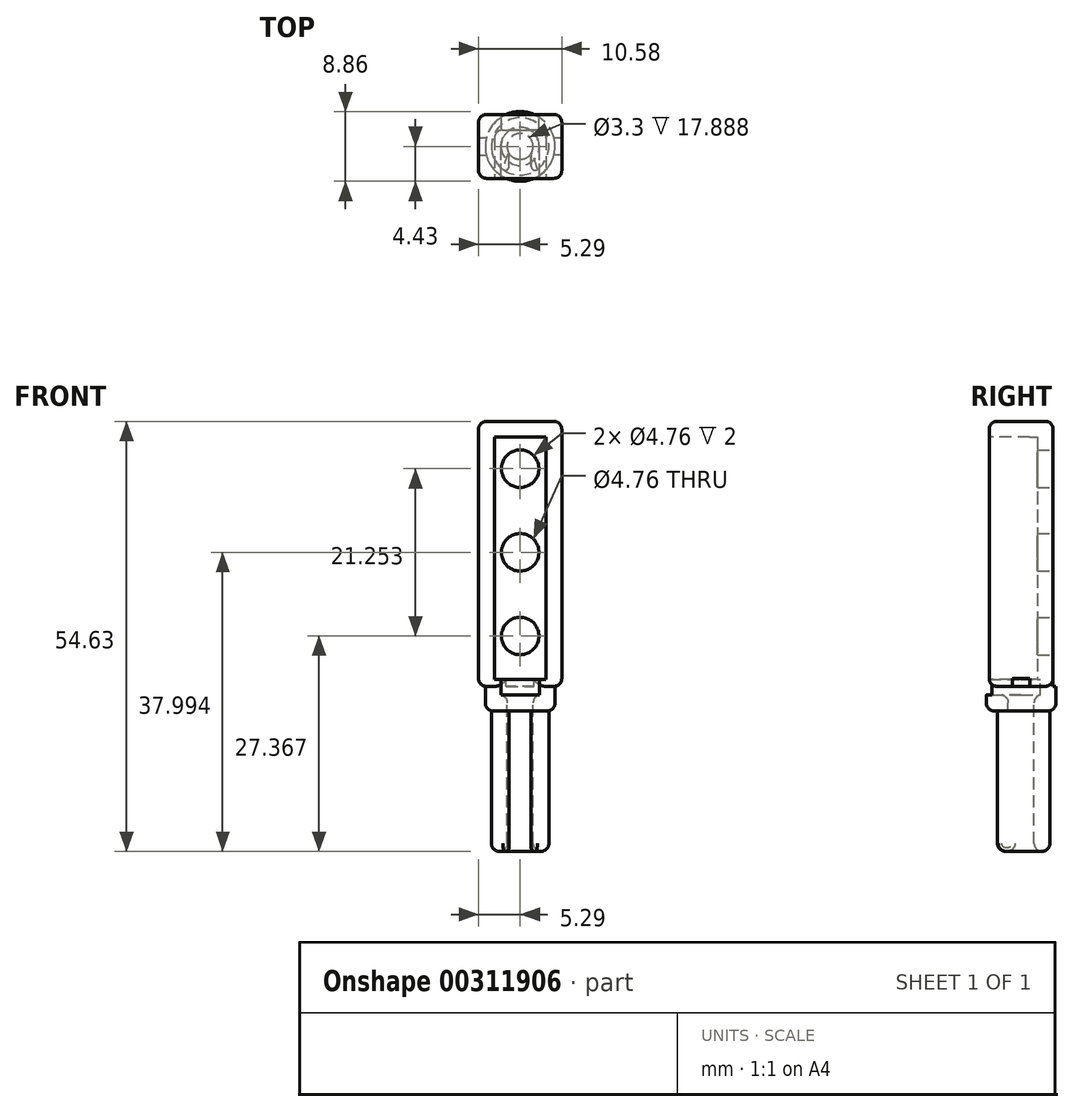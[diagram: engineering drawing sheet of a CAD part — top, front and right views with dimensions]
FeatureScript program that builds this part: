
annotation { "Feature Type Name" : "Feature", "Feature Type Description" : "" }
export const myFeature = defineFeature(function(context is Context, id is Id, definition is map)
    precondition{}
    {
        {
            var Q0;
            Q0=qCreatedBy(makeId("Front.planeOp"),FACE);
            var sketch = newSketch(context, id + "F0", { "sketchPlane" : qUnion([Q0])});
            skLineSegment(sketch, "E0.bottom", {"start": v(-3.3, 14.53) * mm, "end": v(3.3, 14.53) * mm});
            skLineSegment(sketch, "E0.top", {"start": v(-3.29, -16.27) * mm, "end": v(3.29, -16.27) * mm});
            skLineSegment(sketch, "E0.left", {"start": v(-3.3, 14.53) * mm, "end": v(-3.29, -16.27) * mm});
            skLineSegment(sketch, "E0.right", {"start": v(3.3, 14.53) * mm, "end": v(3.29, -16.27) * mm});
            skLineSegment(sketch, "E1.bottom", {"start": v(-2.43, -16.27) * mm, "end": v(2.43, -16.27) * mm});
            skLineSegment(sketch, "E1.top", {"start": v(-2.43, -18.23) * mm, "end": v(2.43, -18.23) * mm});
            skLineSegment(sketch, "E1.left", {"start": v(-2.43, -16.27) * mm, "end": v(-2.43, -18.23) * mm});
            skLineSegment(sketch, "E1.right", {"start": v(2.43, -16.27) * mm, "end": v(2.43, -18.23) * mm});
            skLineSegment(sketch, "E2.bottom", {"start": v(-1.65, -18.23) * mm, "end": v(1.65, -18.23) * mm});
            skLineSegment(sketch, "E2.top", {"start": v(-1.65, -38.23) * mm, "end": v(1.65, -38.23) * mm});
            skLineSegment(sketch, "E2.left", {"start": v(-1.65, -18.23) * mm, "end": v(-1.65, -38.23) * mm});
            skLineSegment(sketch, "E2.right", {"start": v(1.65, -18.23) * mm, "end": v(1.65, -38.23) * mm});
            skLineSegment(sketch, "E3.bottom", {"start": v(-5.29, 16.53) * mm, "end": v(5.3, 16.53) * mm});
            skLineSegment(sketch, "E3.top", {"start": v(-5.29, -17.13) * mm, "end": v(5.3, -17.13) * mm});
            skLineSegment(sketch, "E3.left", {"start": v(-5.3, 16.53) * mm, "end": v(-5.29, -17.13) * mm});
            skLineSegment(sketch, "E3.right", {"start": v(5.29, 16.53) * mm, "end": v(5.3, -17.13) * mm});
            skLineSegment(sketch, "E4.bottom", {"start": v(-4.43, -16.27) * mm, "end": v(4.43, -16.27) * mm});
            skLineSegment(sketch, "E4.top", {"start": v(-4.43, -20.23) * mm, "end": v(4.43, -20.23) * mm});
            skLineSegment(sketch, "E4.left", {"start": v(-4.43, -16.27) * mm, "end": v(-4.43, -20.23) * mm});
            skLineSegment(sketch, "E4.right", {"start": v(4.43, -16.27) * mm, "end": v(4.43, -20.23) * mm});
            skLineSegment(sketch, "E5.bottom", {"start": v(-3.65, -20.23) * mm, "end": v(3.65, -20.23) * mm});
            skLineSegment(sketch, "E5.top", {"start": v(-3.65, -38.1) * mm, "end": v(3.65, -38.1) * mm});
            skLineSegment(sketch, "E5.left", {"start": v(-3.65, -20.23) * mm, "end": v(-3.65, -38.1) * mm});
            skLineSegment(sketch, "E5.right", {"start": v(3.65, -20.23) * mm, "end": v(3.65, -38.1) * mm});
            skLineSegment(sketch, "E6", {"start": v(0, -14.74) * mm, "end": v(0, -39.5) * mm});
            skPoint(sketch, "E6.endSnap0", {"position": v(0, -38.23) * mm});
            skLineSegment(sketch, "E7.bottom", {"start": v(-1.4, -20.23) * mm, "end": v(1.4, -20.23) * mm});
            skLineSegment(sketch, "E7.top", {"start": v(-1.4, -38.1) * mm, "end": v(1.4, -38.1) * mm});
            skLineSegment(sketch, "E7.left", {"start": v(-1.4, -20.23) * mm, "end": v(-1.4, -38.1) * mm});
            skLineSegment(sketch, "E7.right", {"start": v(1.4, -20.23) * mm, "end": v(1.4, -38.1) * mm});
            skSolve(sketch);
        }
        {
            var Q0;
            Q0=makeQuery(id+"F0.imprint","IMPRINT",FACE,{"disambiguationData":[TD([[makeQuery(id+"F0.imprint","IMPRINT",EDGE,{"derivedFrom":sQuery(id+"F0.wireOp",EDGE,"E0.bottom")}),-1.0]])]});
            var Q1;
            Q1=makeQuery(id+"F0.imprint","IMPRINT",FACE,{"disambiguationData":[TD([[makeQuery(id+"F0.imprint","IMPRINT",EDGE,{"derivedFrom":sQuery(id+"F0.wireOp",EDGE,"E0.bottom")}),1.0]])]});
            var Q2;
            {var subQ0=sQuery(id+"F0.wireOp",EDGE,"E4.bottom");var subQ2=sQuery(id+"F0.wireOp",EDGE,"E1.left");var subQ3=makeQuery(id+"F0.imprint","INTERSECT",VERTEX,{"derivedFrom":[subQ2,subQ0]});Q2=makeQuery(id+"F0.imprint","IMPRINT",FACE,{"disambiguationData":[TD([[makeQuery(id+"F0.imprint","IMPRINT",EDGE,{"disambiguationData":[TD([[subQ3,-1.0]])],"derivedFrom":subQ2}),-1.0]])]});}
            var Q3;
            {var subQ0=sQuery(id+"F0.wireOp",EDGE,"E4.bottom");var subQ1=sQuery(id+"F0.wireOp",EDGE,"E1.left");var subQ2=makeQuery(id+"F0.imprint","INTERSECT",VERTEX,{"derivedFrom":[subQ1,subQ0]});Q3=makeQuery(id+"F0.imprint","IMPRINT",FACE,{"disambiguationData":[TD([[makeQuery(id+"F0.imprint","IMPRINT",EDGE,{"disambiguationData":[TD([[subQ2,-1.0]])],"derivedFrom":subQ1}),1.0]])]});}
            var Q4;
            {var subQ0=sQuery(id+"F0.wireOp",EDGE,"E4.bottom");var subQ1=sQuery(id+"F0.wireOp",EDGE,"E1.right");var subQ2=makeQuery(id+"F0.imprint","INTERSECT",VERTEX,{"derivedFrom":[subQ1,subQ0]});Q4=makeQuery(id+"F0.imprint","IMPRINT",FACE,{"disambiguationData":[TD([[makeQuery(id+"F0.imprint","IMPRINT",EDGE,{"disambiguationData":[TD([[subQ2,-1.0]])],"derivedFrom":subQ1}),-1.0]])]});}
            var Q5;
            {var subQ0=sQuery(id+"F0.wireOp",EDGE,"E4.bottom");var subQ6=sQuery(id+"F0.wireOp",EDGE,"E1.right");var subQ8=makeQuery(id+"F0.imprint","INTERSECT",VERTEX,{"derivedFrom":[subQ6,subQ0]});Q5=makeQuery(id+"F0.imprint","IMPRINT",FACE,{"disambiguationData":[TD([[makeQuery(id+"F0.imprint","IMPRINT",EDGE,{"disambiguationData":[TD([[subQ8,-1.0]])],"derivedFrom":subQ6}),1.0]])]});}
            extrude(context, id + "F1", {"entities" : qUnion([Q0, Q1, Q2, Q3, Q4, Q5]), "endBound" : BoundingType.SYMMETRIC, "depth" : 8.12 * mm});
        }
        {
            var Q0;
            Q0=makeQuery(id+"F1.opExtrude","CAP_FACE",FACE,{"disambiguationData":[OSD([sQuery(id+"F0.wireOp",EDGE,"E1.bottom"),sQuery(id+"F0.wireOp",EDGE,"E1.left"),sQuery(id+"F0.wireOp",EDGE,"E1.right"),sQuery(id+"F0.wireOp",EDGE,"E3.bottom"),sQuery(id+"F0.wireOp",EDGE,"E3.top"),sQuery(id+"F0.wireOp",EDGE,"E3.left"),sQuery(id+"F0.wireOp",EDGE,"E3.right")])],"isStart":false});
            var sketch = newSketch(context, id + "F2", { "sketchPlane" : qUnion([Q0])});
            skLineSegment(sketch, "E8.bottom", {"start": v(-3.26, 14.52) * mm, "end": v(3.3, 14.52) * mm});
            skLineSegment(sketch, "E8.top", {"start": v(-3.26, -16.27) * mm, "end": v(3.3, -16.27) * mm});
            skLineSegment(sketch, "E8.left", {"start": v(-3.26, 14.52) * mm, "end": v(-3.26, -16.27) * mm});
            skLineSegment(sketch, "E8.right", {"start": v(3.3, 14.52) * mm, "end": v(3.3, -16.27) * mm});
            skSolve(sketch);
        }
        {
            var Q0;
            Q0=makeQuery(id+"F2.imprint","IMPRINT",FACE,{"disambiguationData":[TD([[makeQuery(id+"F2.imprint","IMPRINT",EDGE,{"derivedFrom":sQuery(id+"F2.wireOp",EDGE,"E8.bottom")}),-1.0]])]});
            extrude(context, id + "F3", {"entities" : qUnion([Q0]), "operationType" : NewBodyOperationType.REMOVE, "oppositeDirection" : true, "depth" : 6.12 * mm});
        }
        {
            var Q0;
            {var subQ3=sQuery(id+"F0.wireOp",EDGE,"E1.left");var subQ5=sQuery(id+"F0.wireOp",EDGE,"E1.top");var subQ6=makeQuery(id+"F0.imprint","INTERSECT",VERTEX,{"derivedFrom":[subQ5,subQ3]});Q0=makeQuery(id+"F0.imprint","IMPRINT",FACE,{"disambiguationData":[TD([[makeQuery(id+"F0.imprint","IMPRINT",EDGE,{"disambiguationData":[TD([[subQ6,1.0]])],"derivedFrom":subQ3}),-1.0]])]});}
            var Q1;
            {var subQ1=sQuery(id+"F0.wireOp",EDGE,"E1.top");var subQ5=sQuery(id+"F0.wireOp",EDGE,"E1.right");var subQ6=makeQuery(id+"F0.imprint","INTERSECT",VERTEX,{"derivedFrom":[subQ1,subQ5]});Q1=makeQuery(id+"F0.imprint","IMPRINT",FACE,{"disambiguationData":[TD([[makeQuery(id+"F0.imprint","IMPRINT",EDGE,{"disambiguationData":[TD([[subQ6,1.0]])],"derivedFrom":subQ5}),1.0]])]});}
            var Q2;
            {var subQ5=sQuery(id+"F0.wireOp",EDGE,"E5.right");Q2=makeQuery(id+"F0.imprint","IMPRINT",FACE,{"disambiguationData":[TD([[makeQuery(id+"F0.imprint","IMPRINT",EDGE,{"derivedFrom":subQ5}),-1.0]])]});}
            var Q3;
            {var subQ5=sQuery(id+"F0.wireOp",EDGE,"E5.left");Q3=makeQuery(id+"F0.imprint","IMPRINT",FACE,{"disambiguationData":[TD([[makeQuery(id+"F0.imprint","IMPRINT",EDGE,{"derivedFrom":subQ5}),1.0]])]});}
            var Q4;
            Q4=sQuery(id+"F0.wireOp",EDGE,"E6");
            revolve(context, id + "F4", {"operationType" : NewBodyOperationType.ADD, "entities" : qUnion([Q0, Q1, Q2, Q3]), "axis" : qUnion([Q4]), "revolveType" : RevolveType.FULL});
        }
        {
            var Q0;
            {var subQ0=sQuery(id+"F0.wireOp",EDGE,"E4.bottom");var subQ1=sQuery(id+"F0.wireOp",EDGE,"E1.left");var subQ2=makeQuery(id+"F0.imprint","INTERSECT",VERTEX,{"derivedFrom":[subQ1,subQ0]});Q0=makeQuery(id+"F0.imprint","IMPRINT",FACE,{"disambiguationData":[TD([[makeQuery(id+"F0.imprint","IMPRINT",EDGE,{"disambiguationData":[TD([[subQ2,-1.0]])],"derivedFrom":subQ1}),1.0]])]});}
            var Q1;
            {var subQ1=sQuery(id+"F0.wireOp",EDGE,"E1.left");var subQ6=sQuery(id+"F0.wireOp",EDGE,"E1.top");var subQ9=makeQuery(id+"F0.imprint","INTERSECT",VERTEX,{"derivedFrom":[subQ6,subQ1]});Q1=makeQuery(id+"F0.imprint","IMPRINT",FACE,{"disambiguationData":[TD([[makeQuery(id+"F0.imprint","IMPRINT",EDGE,{"disambiguationData":[TD([[subQ9,1.0]])],"derivedFrom":subQ1}),1.0]])]});}
            var Q2;
            {var subQ0=sQuery(id+"F0.wireOp",EDGE,"E2.left");var subQ5=sQuery(id+"F0.wireOp",EDGE,"E5.bottom");var subQ6=makeQuery(id+"F0.imprint","INTERSECT",VERTEX,{"derivedFrom":[subQ0,subQ5]});Q2=makeQuery(id+"F0.imprint","IMPRINT",FACE,{"disambiguationData":[TD([[makeQuery(id+"F0.imprint","IMPRINT",EDGE,{"disambiguationData":[TD([[subQ6,-1.0]])],"derivedFrom":subQ5}),1.0]])]});}
            var Q3;
            {var subQ0=sQuery(id+"F0.wireOp",EDGE,"E5.top");var subQ1=sQuery(id+"F0.wireOp",EDGE,"E2.left");var subQ2=makeQuery(id+"F0.imprint","INTERSECT",VERTEX,{"derivedFrom":[subQ1,subQ0]});Q3=makeQuery(id+"F0.imprint","IMPRINT",FACE,{"disambiguationData":[TD([[makeQuery(id+"F0.imprint","IMPRINT",EDGE,{"disambiguationData":[TD([[subQ2,1.0]])],"derivedFrom":subQ1}),1.0]])]});}
            var Q4;
            Q4=sQuery(id+"F0.wireOp",EDGE,"E6");
            revolve(context, id + "F5", {"operationType" : NewBodyOperationType.REMOVE, "entities" : qUnion([Q0, Q1, Q2, Q3]), "axis" : qUnion([Q4]), "revolveType" : RevolveType.FULL, "oppositeDirection" : true});
        }
        {
            var Q0;
            Q0=makeQuery(id+"F3.boolean.opBoolean","COPY",EDGE,{"derivedFrom":makeQuery(id+"F3.opExtrude","CAP_EDGE",EDGE,{"disambiguationData":[OSD([sQuery(id+"F2.wireOp",EDGE,"E8.right")])],"isStart":false})});
            var Q1;
            Q1=makeQuery(id+"F3.boolean.opBoolean","COPY",EDGE,{"derivedFrom":makeQuery(id+"F3.opExtrude","CAP_EDGE",EDGE,{"disambiguationData":[OSD([sQuery(id+"F2.wireOp",EDGE,"E8.left")])],"isStart":false})});
            var Q2;
            Q2=makeQuery(id+"FeuInIf9HhXsNGS_0.boolean.opBoolean","INTERSECT",EDGE,{"derivedFrom":[makeQuery(id+"F4.opRevolve","SWEPT_FACE",FACE,{"disambiguationData":[OSD([sQuery(id+"F0.wireOp",EDGE,"E4.left")])]}),makeQuery(id+"FeuInIf9HhXsNGS_0.opExtrude","SWEPT_FACE",FACE,{"disambiguationData":[OSD([sQuery(id+"F0.wireOp",EDGE,"E2.right")])]})]});
            var Q3;
            Q3=makeQuery(id+"FeuInIf9HhXsNGS_0.boolean.opBoolean","INTERSECT",EDGE,{"derivedFrom":[makeQuery(id+"F4.opRevolve","SWEPT_FACE",FACE,{"disambiguationData":[OSD([sQuery(id+"F0.wireOp",EDGE,"E4.left")])]}),makeQuery(id+"FeuInIf9HhXsNGS_0.opExtrude","SWEPT_FACE",FACE,{"disambiguationData":[OSD([sQuery(id+"F0.wireOp",EDGE,"E2.left")])]})]});
            var Q4;
            Q4=makeQuery(id+"F4.opRevolve","SWEPT_EDGE",EDGE,{"disambiguationData":[OSD([sQuery(id+"F0.wireOp",EDGE,"E5.top"),sQuery(id+"F0.wireOp",EDGE,"E5.left")])]});
            var Q5;
            Q5=makeQuery(id+"F4.opRevolve","SWEPT_EDGE",EDGE,{"disambiguationData":[OSD([sQuery(id+"F0.wireOp",EDGE,"E2.left"),sQuery(id+"F0.wireOp",EDGE,"E5.top")])]});
            var Q6;
            Q6=makeQuery(id+"F4.opRevolve","SWEPT_EDGE",EDGE,{"disambiguationData":[OSD([sQuery(id+"F0.wireOp",EDGE,"E4.top"),sQuery(id+"F0.wireOp",EDGE,"E4.left")])]});
            var Q7;
            Q7=makeQuery(id+"F4.opRevolve","SWEPT_EDGE",EDGE,{"disambiguationData":[OSD([sQuery(id+"F0.wireOp",EDGE,"E1.top"),sQuery(id+"F0.wireOp",EDGE,"E2.bottom"),sQuery(id+"F0.wireOp",EDGE,"E2.left")])]});
            fillet(context, id + "F6", {"entities" : qUnion([Q0, Q1, Q2, Q3, Q4, Q5, Q6, Q7]), "radius" : 1 * mm, "tangentPropagation" : true, "allowEdgeOverflow" : false});
        }
        {
            var Q0;
            {var subQ0=sQuery(id+"F0.wireOp",EDGE,"E4.bottom");var subQ1=sQuery(id+"F0.wireOp",EDGE,"E1.left");var subQ2=makeQuery(id+"F0.imprint","INTERSECT",VERTEX,{"derivedFrom":[subQ1,subQ0]});Q0=makeQuery(id+"F0.imprint","IMPRINT",FACE,{"disambiguationData":[TD([[makeQuery(id+"F0.imprint","IMPRINT",EDGE,{"disambiguationData":[TD([[subQ2,-1.0]])],"derivedFrom":subQ1}),1.0]])]});}
            var Q1;
            {var subQ1=sQuery(id+"F0.wireOp",EDGE,"E1.left");var subQ6=sQuery(id+"F0.wireOp",EDGE,"E1.top");var subQ9=makeQuery(id+"F0.imprint","INTERSECT",VERTEX,{"derivedFrom":[subQ6,subQ1]});Q1=makeQuery(id+"F0.imprint","IMPRINT",FACE,{"disambiguationData":[TD([[makeQuery(id+"F0.imprint","IMPRINT",EDGE,{"disambiguationData":[TD([[subQ9,1.0]])],"derivedFrom":subQ1}),1.0]])]});}
            var Q2;
            {var subQ1=sQuery(id+"F0.wireOp",EDGE,"E1.top");var subQ6=sQuery(id+"F0.wireOp",EDGE,"E1.right");var subQ9=makeQuery(id+"F0.imprint","INTERSECT",VERTEX,{"derivedFrom":[subQ1,subQ6]});Q2=makeQuery(id+"F0.imprint","IMPRINT",FACE,{"disambiguationData":[TD([[makeQuery(id+"F0.imprint","IMPRINT",EDGE,{"disambiguationData":[TD([[subQ9,1.0]])],"derivedFrom":subQ6}),-1.0]])]});}
            var Q3;
            {var subQ0=sQuery(id+"F0.wireOp",EDGE,"E4.bottom");var subQ1=sQuery(id+"F0.wireOp",EDGE,"E1.right");var subQ2=makeQuery(id+"F0.imprint","INTERSECT",VERTEX,{"derivedFrom":[subQ1,subQ0]});Q3=makeQuery(id+"F0.imprint","IMPRINT",FACE,{"disambiguationData":[TD([[makeQuery(id+"F0.imprint","IMPRINT",EDGE,{"disambiguationData":[TD([[subQ2,-1.0]])],"derivedFrom":subQ1}),-1.0]])]});}
            var Q4;
            {var subQ0=sQuery(id+"F0.wireOp",EDGE,"E6");var subQ1=sQuery(id+"F0.wireOp",EDGE,"E2.bottom");var subQ2=makeQuery(id+"F0.imprint","INTERSECT",VERTEX,{"derivedFrom":[subQ1,subQ0]});Q4=makeQuery(id+"F0.imprint","IMPRINT",FACE,{"disambiguationData":[TD([[makeQuery(id+"F0.imprint","IMPRINT",EDGE,{"disambiguationData":[TD([[subQ2,-1.0]])],"derivedFrom":subQ0}),1.0]])]});}
            var Q5;
            {var subQ0=sQuery(id+"F0.wireOp",EDGE,"E6");var subQ1=sQuery(id+"F0.wireOp",EDGE,"E2.bottom");var subQ2=makeQuery(id+"F0.imprint","INTERSECT",VERTEX,{"derivedFrom":[subQ1,subQ0]});Q5=makeQuery(id+"F0.imprint","IMPRINT",FACE,{"disambiguationData":[TD([[makeQuery(id+"F0.imprint","IMPRINT",EDGE,{"disambiguationData":[TD([[subQ2,-1.0]])],"derivedFrom":subQ0}),-1.0]])]});}
            var Q6;
            {var subQ5=sQuery(id+"F0.wireOp",EDGE,"E7.left");Q6=makeQuery(id+"F0.imprint","IMPRINT",FACE,{"disambiguationData":[TD([[makeQuery(id+"F0.imprint","IMPRINT",EDGE,{"derivedFrom":subQ5}),1.0]])]});}
            var Q7;
            {var subQ5=sQuery(id+"F0.wireOp",EDGE,"E7.right");Q7=makeQuery(id+"F0.imprint","IMPRINT",FACE,{"disambiguationData":[TD([[makeQuery(id+"F0.imprint","IMPRINT",EDGE,{"derivedFrom":subQ5}),-1.0]])]});}
            extrude(context, id + "F7", {"entities" : qUnion([Q0, Q1, Q2, Q3, Q4, Q5, Q6, Q7]), "operationType" : NewBodyOperationType.REMOVE, "depth" : 25 * mm});
        }
        {
            var Q0;
            Q0=makeQuery(id+"F7.boolean.opBoolean","INTERSECT",EDGE,{"derivedFrom":[makeQuery(id+"F4.opRevolve","SWEPT_FACE",FACE,{"disambiguationData":[OSD([sQuery(id+"F0.wireOp",EDGE,"E5.left")])]}),makeQuery(id+"F7.opExtrude","SWEPT_FACE",FACE,{"disambiguationData":[OSD([sQuery(id+"F0.wireOp",EDGE,"E7.right")])]})]});
            var Q1;
            Q1=makeQuery(id+"F7.boolean.opBoolean","INTERSECT",EDGE,{"derivedFrom":[makeQuery(id+"F4.opRevolve","SWEPT_FACE",FACE,{"disambiguationData":[OSD([sQuery(id+"F0.wireOp",EDGE,"E5.left")])]}),makeQuery(id+"F7.opExtrude","SWEPT_FACE",FACE,{"disambiguationData":[OSD([sQuery(id+"F0.wireOp",EDGE,"E7.left")])]})]});
            fillet(context, id + "F8", {"entities" : qUnion([Q0, Q1]), "radius" : .5 * mm, "tangentPropagation" : true, "allowEdgeOverflow" : false});
        }
        {
            var Q0;
            Q0=makeQuery(id+"F7.boolean.opBoolean","INTERSECT",EDGE,{"derivedFrom":[makeQuery(id+"F4.opRevolve","SWEPT_FACE",FACE,{"disambiguationData":[OSD([sQuery(id+"F0.wireOp",EDGE,"E4.left")])]}),makeQuery(id+"F7.opExtrude","SWEPT_FACE",FACE,{"disambiguationData":[OSD([sQuery(id+"F0.wireOp",EDGE,"E2.left")])]})]});
            var Q1;
            Q1=makeQuery(id+"F7.boolean.opBoolean","INTERSECT",EDGE,{"derivedFrom":[makeQuery(id+"F4.opRevolve","SWEPT_FACE",FACE,{"disambiguationData":[OSD([sQuery(id+"F0.wireOp",EDGE,"E4.left")])]}),makeQuery(id+"F7.opExtrude","SWEPT_FACE",FACE,{"disambiguationData":[OSD([sQuery(id+"F0.wireOp",EDGE,"E2.right")])]})]});
            var Q2;
            Q2=makeQuery(id+"F1.opExtrude","SWEPT_FACE",FACE,{"disambiguationData":[OSD([sQuery(id+"F0.wireOp",EDGE,"E3.right")])]});
            var Q3;
            {var subQ1=sQuery(id+"F0.wireOp",EDGE,"E3.top");var subQ2=sQuery(id+"F0.wireOp",EDGE,"E3.right");var subQ3=makeQuery(id+"F1.opExtrude","SWEPT_FACE",FACE,{"disambiguationData":[OSD([subQ1])]});var subQ4=makeQuery(id+"F1.opExtrude","CAP_FACE",FACE,{"disambiguationData":[OSD([sQuery(id+"F0.wireOp",EDGE,"E3.bottom"),subQ1,sQuery(id+"F0.wireOp",EDGE,"E3.left"),subQ2])],"isStart":false});Q3=makeQuery(id+"F4.boolean.opBoolean","SPLIT",EDGE,{"disambiguationData":[topologyDisambiguationEdgeConnected([subQ4,subQ3]),TD([makeQuery(id+"F1.opExtrude","SWEPT_FACE",FACE,{"disambiguationData":[OSD([subQ2])]})])],"derivedFrom":makeQuery(id+"F1.opExtrude","CAP_EDGE",EDGE,{"disambiguationData":[OSD([subQ1])],"isStart":false})});}
            var Q4;
            {var subQ1=sQuery(id+"F0.wireOp",EDGE,"E3.top");var subQ2=sQuery(id+"F0.wireOp",EDGE,"E3.left");var subQ3=makeQuery(id+"F1.opExtrude","SWEPT_FACE",FACE,{"disambiguationData":[OSD([subQ1])]});var subQ4=makeQuery(id+"F1.opExtrude","CAP_FACE",FACE,{"disambiguationData":[OSD([sQuery(id+"F0.wireOp",EDGE,"E3.bottom"),subQ1,subQ2,sQuery(id+"F0.wireOp",EDGE,"E3.right")])],"isStart":false});Q4=makeQuery(id+"F4.boolean.opBoolean","SPLIT",EDGE,{"disambiguationData":[topologyDisambiguationEdgeConnected([subQ4,subQ3]),TD([makeQuery(id+"F1.opExtrude","SWEPT_FACE",FACE,{"disambiguationData":[OSD([subQ2])]})])],"derivedFrom":makeQuery(id+"F1.opExtrude","CAP_EDGE",EDGE,{"disambiguationData":[OSD([subQ1])],"isStart":false})});}
            var Q5;
            Q5=makeQuery(id+"F1.opExtrude","SWEPT_FACE",FACE,{"disambiguationData":[OSD([sQuery(id+"F0.wireOp",EDGE,"E3.left")])]});
            var Q6;
            {var subQ0=sQuery(id+"F0.wireOp",EDGE,"E3.left");var subQ2=sQuery(id+"F0.wireOp",EDGE,"E3.top");var subQ3=makeQuery(id+"F1.opExtrude","SWEPT_FACE",FACE,{"disambiguationData":[OSD([subQ2])]});var subQ4=makeQuery(id+"F1.opExtrude","CAP_FACE",FACE,{"disambiguationData":[OSD([sQuery(id+"F0.wireOp",EDGE,"E3.bottom"),subQ2,subQ0,sQuery(id+"F0.wireOp",EDGE,"E3.right")])],"isStart":true});Q6=makeQuery(id+"F4.boolean.opBoolean","SPLIT",EDGE,{"disambiguationData":[topologyDisambiguationEdgeConnected([subQ4,subQ3]),TD([makeQuery(id+"F1.opExtrude","SWEPT_FACE",FACE,{"disambiguationData":[OSD([subQ0])]})])],"derivedFrom":makeQuery(id+"F1.opExtrude","CAP_EDGE",EDGE,{"disambiguationData":[OSD([subQ2])],"isStart":true})});}
            var Q7;
            {var subQ0=sQuery(id+"F0.wireOp",EDGE,"E3.right");var subQ1=sQuery(id+"F0.wireOp",EDGE,"E3.top");var subQ2=makeQuery(id+"F1.opExtrude","SWEPT_FACE",FACE,{"disambiguationData":[OSD([subQ1])]});var subQ4=makeQuery(id+"F1.opExtrude","CAP_FACE",FACE,{"disambiguationData":[OSD([sQuery(id+"F0.wireOp",EDGE,"E3.bottom"),subQ1,sQuery(id+"F0.wireOp",EDGE,"E3.left"),subQ0])],"isStart":true});Q7=makeQuery(id+"F4.boolean.opBoolean","SPLIT",EDGE,{"disambiguationData":[topologyDisambiguationEdgeConnected([subQ4,subQ2]),TD([makeQuery(id+"F1.opExtrude","SWEPT_FACE",FACE,{"disambiguationData":[OSD([subQ0])]})])],"derivedFrom":makeQuery(id+"F1.opExtrude","CAP_EDGE",EDGE,{"disambiguationData":[OSD([subQ1])],"isStart":true})});}
            var Q8;
            {var subQ0=sQuery(id+"F0.wireOp",EDGE,"E3.top");Q8=makeQuery(id+"F4.boolean.opBoolean","SPLIT",EDGE,{"disambiguationData":[topologyDisambiguationEdgeConnected([makeQuery(id+"F1.opExtrude","CAP_FACE",FACE,{"disambiguationData":[OSD([sQuery(id+"F0.wireOp",EDGE,"E3.bottom"),subQ0,sQuery(id+"F0.wireOp",EDGE,"E3.left"),sQuery(id+"F0.wireOp",EDGE,"E3.right")])],"isStart":true}),makeQuery(id+"F4.opRevolve","SWEPT_FACE",FACE,{"disambiguationData":[OSD([subQ0]),TDD([makeQuery(id+"F0.imprint","IMPRINT",EDGE,{"disambiguationData":[TD([[makeQuery(id+"F0.imprint","INTERSECT",VERTEX,{"derivedFrom":[subQ0,sQuery(id+"F0.wireOp",EDGE,"E4.left")]}),-1.0]])],"derivedFrom":subQ0})])]})])],"derivedFrom":makeQuery(id+"F1.opExtrude","CAP_EDGE",EDGE,{"disambiguationData":[OSD([subQ0])],"isStart":true})});}
            var Q9;
            Q9=makeQuery(id+"F1.opExtrude","CAP_EDGE",EDGE,{"disambiguationData":[OSD([sQuery(id+"F0.wireOp",EDGE,"E3.bottom")])],"isStart":true});
            var Q10;
            Q10=makeQuery(id+"F1.opExtrude","CAP_EDGE",EDGE,{"disambiguationData":[OSD([sQuery(id+"F0.wireOp",EDGE,"E3.bottom")])],"isStart":false});
            fillet(context, id + "F9", {"entities" : qUnion([Q0, Q1, Q2, Q3, Q4, Q5, Q6, Q7, Q8, Q9, Q10]), "radius" : 1 * mm, "tangentPropagation" : true, "allowEdgeOverflow" : false});
        }
        {
            var Q0;
            Q0=makeQuery(id+"F1.opExtrude","CAP_FACE",FACE,{"disambiguationData":[OSD([sQuery(id+"F0.wireOp",EDGE,"E3.bottom"),sQuery(id+"F0.wireOp",EDGE,"E3.top"),sQuery(id+"F0.wireOp",EDGE,"E3.left"),sQuery(id+"F0.wireOp",EDGE,"E3.right")])],"isStart":true});
            var sketch = newSketch(context, id + "F10", { "sketchPlane" : qUnion([Q0])});
            skCircle(sketch, "E9", {"center": v(0, -10.73) * mm, "radius": 2.38 * mm});
            skCircle(sketch, "E10.1.0.0", {"center": v(0, -0.1) * mm, "radius": 2.38 * mm});
            skCircle(sketch, "E10.2.0.0", {"center": v(0, 10.52) * mm, "radius": 2.38 * mm});
            skLineSegment(sketch, "E10.direction1", {"start": v(0, -10.73) * mm, "end": v(0, -0.1) * mm, "construction": true});
            skSolve(sketch);
        }
        {
            var Q0;
            Q0 = qSketchRegion(id + "F10", true);
            extrude(context, id + "F11", {"entities" : qUnion([Q0]), "operationType" : NewBodyOperationType.REMOVE, "oppositeDirection" : true, "depth" : 25 * mm});
        }
    });
